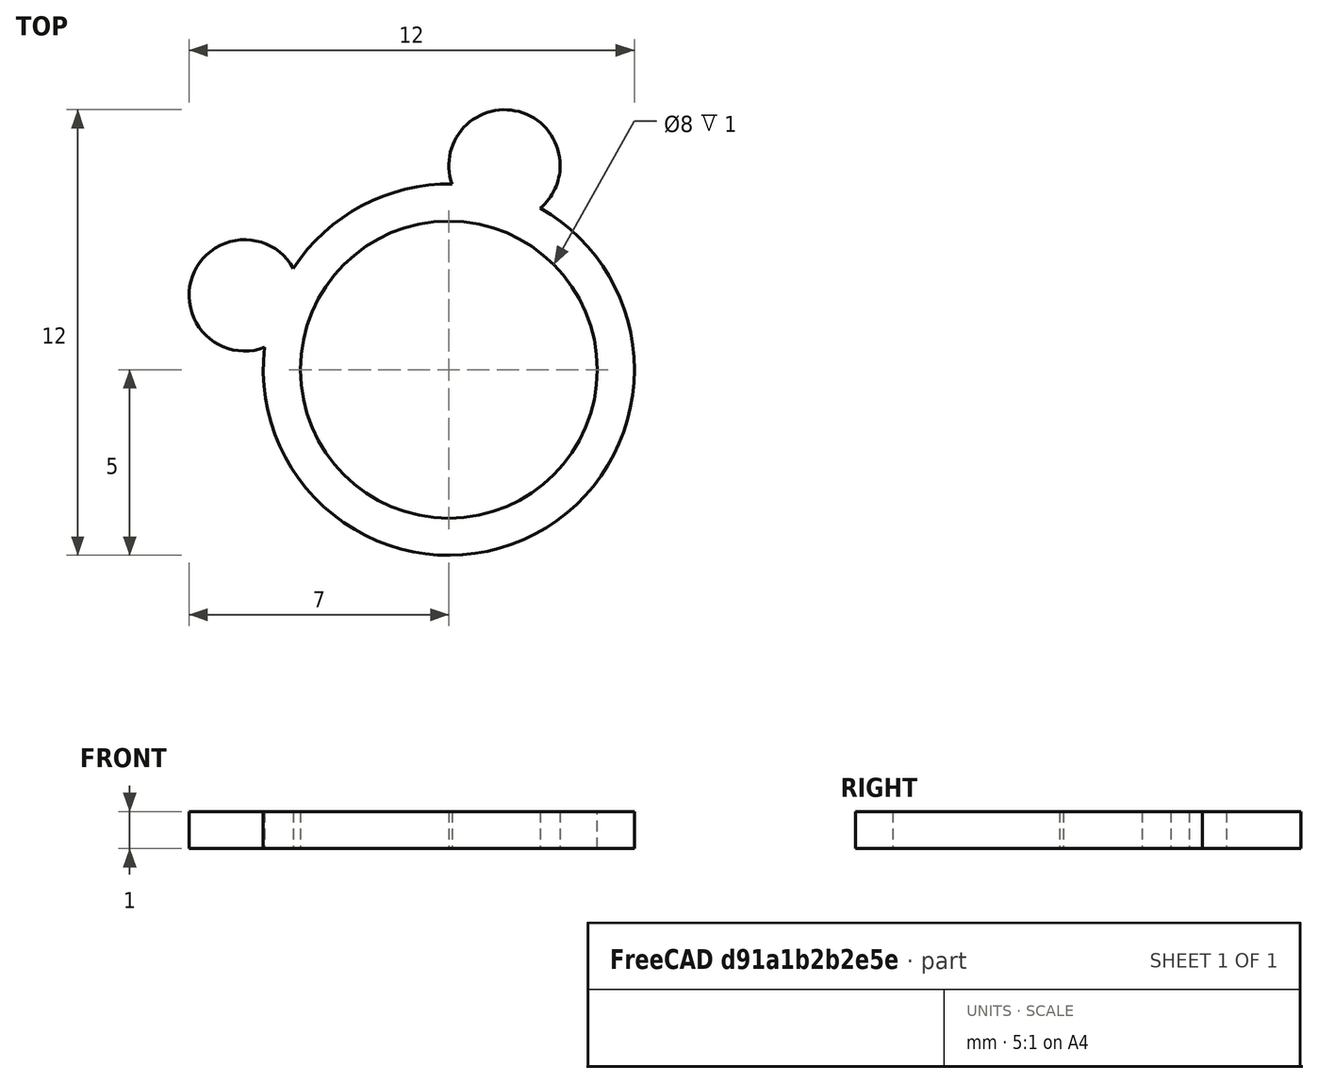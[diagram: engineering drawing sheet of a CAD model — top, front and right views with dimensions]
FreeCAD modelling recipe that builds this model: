
FCSTD DOCUMENT  (FreeCAD 1.0R38806 (Git))
Label: anillo_osito
License: All rights reserved
LicenseURL: https://en.wikipedia.org/wiki/All_rights_reserved
objects: Part::Cylinder×4, Part::Cut×1, Part::MultiFuse×1
note: 6 computed .brp shape members not serialized (recipe doc carries the construction recipe); baked Part::Feature solids carry a one-line shape summary decoded from their .brp

FEATURE [Part::Cylinder] Cylinder
  Angle = 360
  AttacherType = Attacher::AttachEngine3D
  FirstAngle = 0
  Height = 1
  Radius = 5
  SecondAngle = 0
FEATURE [Part::Cylinder] Cylinder001
  Angle = 360
  AttacherType = Attacher::AttachEngine3D
  FirstAngle = 0
  Height = 10
  Placement = pos=(0,0,-5) rot=(0,0,1;0rad)
  Radius = 4
  SecondAngle = 0
FEATURE [Part::Cut] Cut
  Base = -> Cylinder
  Refine = true
  Tool = -> Cylinder001
FEATURE [Part::Cylinder] Cylinder002
  Angle = 360
  AttacherType = Attacher::AttachEngine3D
  FirstAngle = 0
  Height = 1
  Placement = pos=(-5.5,2,0) rot=(0,0,1;0rad)
  Radius = 1.5
  SecondAngle = 0
FEATURE [Part::Cylinder] Cylinder003
  Angle = 360
  AttacherType = Attacher::AttachEngine3D
  FirstAngle = 0
  Height = 1
  Placement = pos=(1.5,5.5,0) rot=(0,0,1;0rad)
  Radius = 1.5
  SecondAngle = 0
FEATURE [Part::MultiFuse] Fusion
  Refine = true
  Shapes = -> [Cylinder002,Cylinder003,Cut]
